# Revit family: ElectricalEquipment_Hager_TPNLighting&Power_HagerTPNDualExtBoxMountedIncomers(withdoor)
name_source: partatom
category: Electrical Equipment
revit_build: Autodesk Revit 2015 (Build: 20160512_1515(x64)
units: mm (PartAtom-declared; Revit-internal decimal feet)

## types (1)
- TPN Dual Ext Box Mounted Incomer 125A Metered KWH Modbus
    Busbar Rating = 125 A
    CE Approval = Yes
    Colour = BS4800:2011 00A01 Oyster Grey
    Default Elevation = 1200 mm
    Description = Invicta 3 TPN Dual Meter 125A Swd KWH Modbus
    Design Country = China
    Door = 46 mm  [stored 0.150919 ft]
    Door Curve = 962 mm  [stored 3.15617 ft]
    Door Type = Twin Glazed Door
    EAN = 5015652252450
    Enclosure Rating = IP3X
    Frequency = 50 Hz
    Hager Catalogue Ref = JKD125BKWM
    Location = Indoors
    Location of Manufacturer = Telford, TF1 7FT
    MCB Rating = 63 A
    Mains Type = 3 phase
    Manufacturer = Hager UK Ltd
    Manufacturer Country = United Kingdom
    Manufacturer Website = www.hager.co.uk
    Max #3 Pole Breakers = 0
    Model = JKD125BKWM
    Neutral Rating = 100.00%
    Number of Poles = 4
    Outging Ways (TP) = 0
    Overall Height = 133 mm  [stored 0.436352 ft]
    Overall Width = 915 mm  [stored 3.00197 ft]
    Packaging Recyclable = Yes
    Packaging Weight = 1.00 kg
    Pollution Degree = 2
    Product Description = Invicta 3 TPN Dual Meter 125A Swd KWH Modbus
    Product Family = TPN Dual Ext Box Mounted Incomer w Door
    Product Group = TPN
    Product Literature = www.hager.co.uk/?artnr=JKD125BKWM
    Product Range = Invicta 3 TPN Dual Meter Incomer
    Product Weight = 32.00 kg
    Reference Standard = BS EN 61439-3
    Revision = 2
    Shape = Rectangular
    Supply Phase = 1,3
    Type = Electrical Fixture
    Type Comments = Mounted directly below JK1 primary Distribution Board
    URL = www.hager.co.uk
    Ui Rating = 690 V
    Uimp Rating = 4000 V
    Voltage = 415
    Warranty ID = 24 Months

note: [stored X ft] marks values corroborated as IEEE doubles in the binary element streams (Revit-internal decimal feet)

## geometry (parser evidence)
native form markers: Sweep x3
no freeform markers — native parametric forms only
